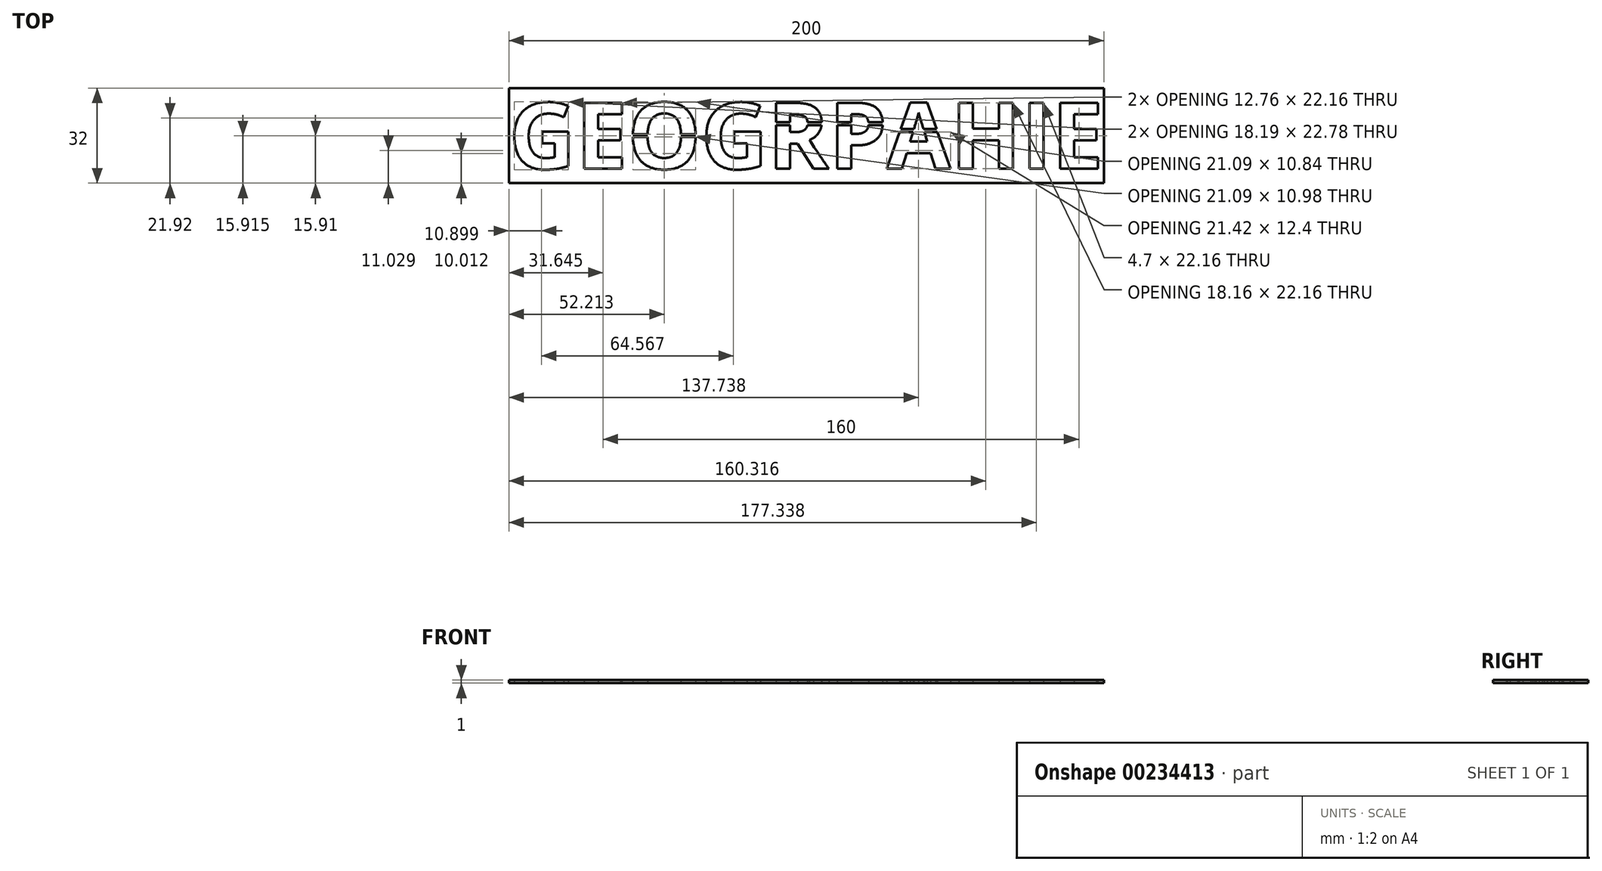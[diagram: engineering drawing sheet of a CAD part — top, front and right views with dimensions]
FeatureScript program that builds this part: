
annotation { "Feature Type Name" : "Feature", "Feature Type Description" : "" }
export const myFeature = defineFeature(function(context is Context, id is Id, definition is map)
    precondition{}
    {
        {
            var Q0;
            Q0=qCreatedBy(makeId("Top.planeOp"),FACE);
            var sketch = newSketch(context, id + "F0", { "sketchPlane" : qUnion([Q0])});
            skLineSegment(sketch, "E0.bottom", {"start": v(0, 0) * mm, "end": v(200, 0) * mm});
            skLineSegment(sketch, "E0.top", {"start": v(0, 32) * mm, "end": v(200, 32) * mm});
            skLineSegment(sketch, "E0.left", {"start": v(0, 0) * mm, "end": v(0, 32) * mm});
            skLineSegment(sketch, "E0.right", {"start": v(200, 0) * mm, "end": v(200, 32) * mm});
            skText(sketch, "E1", { "text": "GEOGRPAHIE", "fontName": "OpenSans-Bold.ttf"});
            skPoint(sketch, "E2", {"position": v(0, 16) * mm});
            skPoint(sketch, "E3", {"position": v(22.5, 32) * mm});
            skPoint(sketch, "E4", {"position": v(40, 32) * mm});
            skPoint(sketch, "E5", {"position": v(64.5, 32) * mm});
            skPoint(sketch, "E6", {"position": v(87, 32) * mm});
            skPoint(sketch, "E7", {"position": v(108.5, 32) * mm});
            skPoint(sketch, "E8", {"position": v(126.5, 32) * mm});
            skPoint(sketch, "E9", {"position": v(150, 32) * mm});
            skPoint(sketch, "E10", {"position": v(172, 32) * mm});
            skPoint(sketch, "E11", {"position": v(182.5, 32) * mm});
            skLineSegment(sketch, "E12", {"start": v(22.5, 32) * mm, "end": v(22.5, 0) * mm, "construction": true});
            skLineSegment(sketch, "E13", {"start": v(40, 32) * mm, "end": v(40, 0) * mm, "construction": true});
            skLineSegment(sketch, "E14", {"start": v(64.5, 32) * mm, "end": v(64.5, 0) * mm, "construction": true});
            skPoint(sketch, "E15", {"position": v(22.5, 16) * mm});
            skPoint(sketch, "E16", {"position": v(40, 16) * mm});
            skPoint(sketch, "E17", {"position": v(64.5, 16) * mm});
            skLineSegment(sketch, "E18", {"start": v(40, 16.5) * mm, "end": v(64.5, 16.5) * mm});
            skLineSegment(sketch, "E19", {"start": v(40, 16) * mm, "end": v(64.5, 16) * mm, "construction": true});
            skLineSegment(sketch, "E20.MirrorCS", {"start": v(40, 15.5) * mm, "end": v(64.5, 15.5) * mm});
            skLineSegment(sketch, "E21", {"start": v(87, 32) * mm, "end": v(87, 0) * mm, "construction": true});
            skLineSegment(sketch, "E22", {"start": v(108.5, 32) * mm, "end": v(108.5, 0) * mm, "construction": true});
            skLineSegment(sketch, "E23", {"start": v(126.5, 32) * mm, "end": v(126.5, 0) * mm, "construction": true});
            skLineSegment(sketch, "E24", {"start": v(150, 32) * mm, "end": v(150, 0) * mm, "construction": true});
            skLineSegment(sketch, "E25", {"start": v(172, 32) * mm, "end": v(172, 0) * mm, "construction": true});
            skLineSegment(sketch, "E26", {"start": v(182.5, 32) * mm, "end": v(182.5, 0) * mm, "construction": true});
            skLineSegment(sketch, "E27", {"start": v(87, 20.55) * mm, "end": v(108.5, 20.55) * mm});
            skLineSegment(sketch, "E28", {"start": v(87, 20.05) * mm, "end": v(108.5, 20.05) * mm, "construction": true});
            skLineSegment(sketch, "E29.MirrorCS", {"start": v(87, 19.55) * mm, "end": v(108.5, 19.55) * mm});
            skLineSegment(sketch, "E30", {"start": v(108.5, 19.97) * mm, "end": v(126.5, 19.97) * mm, "construction": true});
            skLineSegment(sketch, "E31", {"start": v(108.5, 20.47) * mm, "end": v(126.5, 20.47) * mm});
            skLineSegment(sketch, "E32.MirrorCS", {"start": v(108.5, 19.47) * mm, "end": v(126.5, 19.47) * mm});
            skLineSegment(sketch, "E33", {"start": v(126.5, 17.73) * mm, "end": v(150, 17.73) * mm, "construction": true});
            skLineSegment(sketch, "E34", {"start": v(126.5, 18.23) * mm, "end": v(150, 18.23) * mm});
            skLineSegment(sketch, "E35.MirrorCS", {"start": v(126.5, 17.23) * mm, "end": v(150, 17.23) * mm});
            const initialGuessF0  = {"E1": [0, 0.00483, 1, 0, 0.02235]};
            skSetInitialGuess(sketch, initialGuessF0);
            skSolve(sketch);
        }
        {
            var Q0;
            Q0 = qSketchRegion(id + "F0", true);
            var Q1;
            {var subQ8=sQuery(id+"F0.wireOp",EDGE,"E1.sketch_text.stroke-45");Q1=makeQuery(id+"F0.imprint","IMPRINT",FACE,{"disambiguationData":[TD([[makeQuery(id+"F0.imprint","IMPRINT",EDGE,{"derivedFrom":subQ8}),1.0]])]});}
            var Q2;
            {var subQ1=sQuery(id+"F0.wireOp",EDGE,"E1.sketch_text.stroke-67");Q2=makeQuery(id+"F0.imprint","IMPRINT",FACE,{"disambiguationData":[TD([[makeQuery(id+"F0.imprint","IMPRINT",EDGE,{"derivedFrom":subQ1}),1.0]])]});}
            var Q3;
            {var subQ1=sQuery(id+"F0.wireOp",EDGE,"E1.sketch_text.stroke-64");Q3=makeQuery(id+"F0.imprint","IMPRINT",FACE,{"disambiguationData":[TD([[makeQuery(id+"F0.imprint","IMPRINT",EDGE,{"derivedFrom":subQ1}),1.0]])]});}
            var Q4;
            Q4=makeQuery(id+"F0.imprint","IMPRINT",FACE,{"disambiguationData":[TD([[makeQuery(id+"F0.imprint","IMPRINT",EDGE,{"derivedFrom":sQuery(id+"F0.wireOp",EDGE,"E1.sketch_text.stroke-83")}),1.0]])]});
            var Q5;
            Q5=makeQuery(id+"F0.imprint","IMPRINT",FACE,{"disambiguationData":[TD([[makeQuery(id+"F0.imprint","IMPRINT",EDGE,{"derivedFrom":sQuery(id+"F0.wireOp",EDGE,"E1.sketch_text.stroke-107")}),1.0]])]});
            var Q6;
            {var subQ0=sQuery(id+"F0.wireOp",EDGE,"E1.sketch_text.stroke-38");var subQ1=sQuery(id+"F0.wireOp",EDGE,"E1.sketch_text.stroke-31");var subQ2=makeQuery(id+"F0.imprint","INTERSECT",VERTEX,{"derivedFrom":[subQ1,subQ0]});Q6=makeQuery(id+"F0.imprint","IMPRINT",FACE,{"disambiguationData":[TD([[makeQuery(id+"F0.imprint","IMPRINT",EDGE,{"disambiguationData":[TD([[subQ2,-1.0]])],"derivedFrom":subQ1}),1.0]])]});}
            var Q7;
            {var subQ0=sQuery(id+"F0.wireOp",EDGE,"E1.sketch_text.stroke-59");Q7=makeQuery(id+"F0.imprint","IMPRINT",FACE,{"disambiguationData":[TD([[makeQuery(id+"F0.imprint","IMPRINT",EDGE,{"derivedFrom":subQ0}),1.0]])]});}
            var Q8;
            {var subQ9=sQuery(id+"F0.wireOp",EDGE,"E1.sketch_text.stroke-27");Q8=makeQuery(id+"F0.imprint","IMPRINT",FACE,{"disambiguationData":[TD([[makeQuery(id+"F0.imprint","IMPRINT",EDGE,{"derivedFrom":subQ9}),1.0]])]});}
            var Q9;
            {var subQ11=sQuery(id+"F0.wireOp",EDGE,"E1.sketch_text.stroke-0");Q9=makeQuery(id+"F0.imprint","IMPRINT",FACE,{"disambiguationData":[TD([[makeQuery(id+"F0.imprint","IMPRINT",EDGE,{"derivedFrom":subQ11}),1.0]])]});}
            var Q10;
            {var subQ5=sQuery(id+"F0.wireOp",EDGE,"E1.sketch_text.stroke-14");Q10=makeQuery(id+"F0.imprint","IMPRINT",FACE,{"disambiguationData":[TD([[makeQuery(id+"F0.imprint","IMPRINT",EDGE,{"derivedFrom":subQ5}),1.0]])]});}
            var Q11;
            {var subQ0=sQuery(id+"F0.wireOp",EDGE,"E1.sketch_text.stroke-44");var subQ1=sQuery(id+"F0.wireOp",EDGE,"E1.sketch_text.stroke-39");var subQ2=makeQuery(id+"F0.imprint","INTERSECT",VERTEX,{"derivedFrom":[subQ1,subQ0]});Q11=makeQuery(id+"F0.imprint","IMPRINT",FACE,{"disambiguationData":[TD([[makeQuery(id+"F0.imprint","IMPRINT",EDGE,{"disambiguationData":[TD([[subQ2,-1.0]])],"derivedFrom":subQ1}),1.0]])]});}
            var Q12;
            {var subQ0=sQuery(id+"F0.wireOp",EDGE,"E1.sketch_text.stroke-43");Q12=makeQuery(id+"F0.imprint","IMPRINT",FACE,{"disambiguationData":[TD([[makeQuery(id+"F0.imprint","IMPRINT",EDGE,{"derivedFrom":subQ0}),1.0]])]});}
            var Q13;
            {var subQ0=sQuery(id+"F0.wireOp",EDGE,"E1.sketch_text.stroke-40");Q13=makeQuery(id+"F0.imprint","IMPRINT",FACE,{"disambiguationData":[TD([[makeQuery(id+"F0.imprint","IMPRINT",EDGE,{"derivedFrom":subQ0}),1.0]])]});}
            var Q14;
            {var subQ1=sQuery(id+"F0.wireOp",EDGE,"E1.sketch_text.stroke-12");var subQ5=sQuery(id+"F0.wireOp",EDGE,"E1.sketch_text.stroke-13");var subQ6=makeQuery(id+"F0.imprint","INTERSECT",VERTEX,{"derivedFrom":[subQ1,subQ5]});Q14=makeQuery(id+"F0.imprint","IMPRINT",FACE,{"disambiguationData":[TD([[makeQuery(id+"F0.imprint","IMPRINT",EDGE,{"disambiguationData":[TD([[subQ6,1.0]])],"derivedFrom":subQ1}),1.0]])]});}
            var Q15;
            {var subQ0=sQuery(id+"F0.wireOp",EDGE,"Y53SOWeo-wKMP-z9sr-oB1W-zrnG9GxjqqMA");var subQ1=sQuery(id+"F0.wireOp",EDGE,"E1.sketch_text.stroke-1");var subQ2=makeQuery(id+"F0.imprint","INTERSECT",VERTEX,{"derivedFrom":[subQ1,subQ0]});Q15=makeQuery(id+"F0.imprint","IMPRINT",FACE,{"disambiguationData":[TD([[makeQuery(id+"F0.imprint","IMPRINT",EDGE,{"disambiguationData":[TD([[subQ2,-1.0]])],"derivedFrom":subQ1}),1.0]])]});}
            var Q16;
            {var subQ3=sQuery(id+"F0.wireOp",EDGE,"Y53SOWeo-wKMP-z9sr-oB1W-zrnG9GxjqqMA");var subQ6=sQuery(id+"F0.wireOp",EDGE,"E1.sketch_text.stroke-26");var subQ9=makeQuery(id+"F0.imprint","INTERSECT",VERTEX,{"derivedFrom":[subQ6,subQ3]});Q16=makeQuery(id+"F0.imprint","IMPRINT",FACE,{"disambiguationData":[TD([[makeQuery(id+"F0.imprint","IMPRINT",EDGE,{"disambiguationData":[TD([[subQ9,-1.0]])],"derivedFrom":subQ6}),1.0]])]});}
            var Q17;
            {var subQ1=sQuery(id+"F0.wireOp",EDGE,"E1.sketch_text.stroke-57");var subQ7=sQuery(id+"F0.wireOp",EDGE,"E1.sketch_text.stroke-58");var subQ8=makeQuery(id+"F0.imprint","INTERSECT",VERTEX,{"derivedFrom":[subQ1,subQ7]});Q17=makeQuery(id+"F0.imprint","IMPRINT",FACE,{"disambiguationData":[TD([[makeQuery(id+"F0.imprint","IMPRINT",EDGE,{"disambiguationData":[TD([[subQ8,1.0]])],"derivedFrom":subQ1}),1.0]])]});}
            var Q18;
            {var subQ0=sQuery(id+"F0.wireOp",EDGE,"Y53SOWeo-wKMP-z9sr-oB1W-zrnG9GxjqqMA");var subQ1=sQuery(id+"F0.wireOp",EDGE,"E1.sketch_text.stroke-46");var subQ2=makeQuery(id+"F0.imprint","INTERSECT",VERTEX,{"derivedFrom":[subQ1,subQ0]});Q18=makeQuery(id+"F0.imprint","IMPRINT",FACE,{"disambiguationData":[TD([[makeQuery(id+"F0.imprint","IMPRINT",EDGE,{"disambiguationData":[TD([[subQ2,-1.0]])],"derivedFrom":subQ1}),1.0]])]});}
            var Q19;
            {var subQ0=sQuery(id+"F0.wireOp",EDGE,"E1.sketch_text.stroke-38");var subQ1=sQuery(id+"F0.wireOp",EDGE,"E1.sketch_text.stroke-31");var subQ2=makeQuery(id+"F0.imprint","INTERSECT",VERTEX,{"derivedFrom":[subQ1,subQ0]});Q19=makeQuery(id+"F0.imprint","IMPRINT",FACE,{"disambiguationData":[TD([[makeQuery(id+"F0.imprint","IMPRINT",EDGE,{"disambiguationData":[TD([[subQ2,-1.0]])],"derivedFrom":subQ1}),-1.0]])]});}
            var Q20;
            {var subQ5=sQuery(id+"F0.wireOp",EDGE,"E1.sketch_text.stroke-35");var subQ6=sQuery(id+"F0.wireOp",EDGE,"E1.sketch_text.stroke-34");var subQ7=makeQuery(id+"F0.imprint","INTERSECT",VERTEX,{"derivedFrom":[subQ6,subQ5]});Q20=makeQuery(id+"F0.imprint","IMPRINT",FACE,{"disambiguationData":[TD([[makeQuery(id+"F0.imprint","IMPRINT",EDGE,{"disambiguationData":[TD([[subQ7,1.0]])],"derivedFrom":subQ6}),-1.0]])]});}
            var Q21;
            {var subQ0=sQuery(id+"F0.wireOp",EDGE,"E27");var subQ1=sQuery(id+"F0.wireOp",EDGE,"E1.sketch_text.stroke-70");var subQ2=makeQuery(id+"F0.imprint","INTERSECT",VERTEX,{"derivedFrom":[subQ1,subQ0]});Q21=makeQuery(id+"F0.imprint","IMPRINT",FACE,{"disambiguationData":[TD([[makeQuery(id+"F0.imprint","IMPRINT",EDGE,{"disambiguationData":[TD([[subQ2,-1.0]])],"derivedFrom":subQ1}),-1.0]])]});}
            var Q22;
            {var subQ3=sQuery(id+"F0.wireOp",EDGE,"E1.sketch_text.stroke-67");var subQ7=sQuery(id+"F0.wireOp",EDGE,"E1.sketch_text.stroke-66");var subQ8=makeQuery(id+"F0.imprint","INTERSECT",VERTEX,{"derivedFrom":[subQ7,subQ3]});Q22=makeQuery(id+"F0.imprint","IMPRINT",FACE,{"disambiguationData":[TD([[makeQuery(id+"F0.imprint","IMPRINT",EDGE,{"disambiguationData":[TD([[subQ8,1.0]])],"derivedFrom":subQ7}),-1.0]])]});}
            var Q23;
            {var subQ1=sQuery(id+"F0.wireOp",EDGE,"E1.sketch_text.stroke-86");var subQ7=sQuery(id+"F0.wireOp",EDGE,"E1.sketch_text.stroke-85");var subQ8=makeQuery(id+"F0.imprint","INTERSECT",VERTEX,{"derivedFrom":[subQ7,subQ1]});Q23=makeQuery(id+"F0.imprint","IMPRINT",FACE,{"disambiguationData":[TD([[makeQuery(id+"F0.imprint","IMPRINT",EDGE,{"disambiguationData":[TD([[subQ8,1.0]])],"derivedFrom":subQ7}),1.0]])]});}
            var Q24;
            {var subQ6=sQuery(id+"F0.wireOp",EDGE,"E1.sketch_text.stroke-87");Q24=makeQuery(id+"F0.imprint","IMPRINT",FACE,{"disambiguationData":[TD([[makeQuery(id+"F0.imprint","IMPRINT",EDGE,{"derivedFrom":subQ6}),1.0]])]});}
            var Q25;
            {var subQ0=sQuery(id+"F0.wireOp",EDGE,"E31");var subQ1=sQuery(id+"F0.wireOp",EDGE,"E1.sketch_text.stroke-89");var subQ2=makeQuery(id+"F0.imprint","INTERSECT",VERTEX,{"derivedFrom":[subQ1,subQ0]});Q25=makeQuery(id+"F0.imprint","IMPRINT",FACE,{"disambiguationData":[TD([[makeQuery(id+"F0.imprint","IMPRINT",EDGE,{"disambiguationData":[TD([[subQ2,-1.0]])],"derivedFrom":subQ1}),-1.0]])]});}
            var Q26;
            {var subQ5=sQuery(id+"F0.wireOp",EDGE,"E1.sketch_text.stroke-86");var subQ6=sQuery(id+"F0.wireOp",EDGE,"E1.sketch_text.stroke-85");var subQ7=makeQuery(id+"F0.imprint","INTERSECT",VERTEX,{"derivedFrom":[subQ6,subQ5]});Q26=makeQuery(id+"F0.imprint","IMPRINT",FACE,{"disambiguationData":[TD([[makeQuery(id+"F0.imprint","IMPRINT",EDGE,{"disambiguationData":[TD([[subQ7,1.0]])],"derivedFrom":subQ6}),-1.0]])]});}
            var Q27;
            {var subQ0=sQuery(id+"F0.wireOp",EDGE,"E35.MirrorCS");var subQ1=sQuery(id+"F0.wireOp",EDGE,"E1.sketch_text.stroke-103");var subQ2=makeQuery(id+"F0.imprint","INTERSECT",VERTEX,{"derivedFrom":[subQ1,subQ0]});Q27=makeQuery(id+"F0.imprint","IMPRINT",FACE,{"disambiguationData":[TD([[makeQuery(id+"F0.imprint","IMPRINT",EDGE,{"disambiguationData":[TD([[subQ2,-1.0]])],"derivedFrom":subQ1}),-1.0]])]});}
            var Q28;
            {var subQ0=sQuery(id+"F0.wireOp",EDGE,"E34");var subQ1=sQuery(id+"F0.wireOp",EDGE,"E1.sketch_text.stroke-105");var subQ2=makeQuery(id+"F0.imprint","INTERSECT",VERTEX,{"derivedFrom":[subQ1,subQ0]});Q28=makeQuery(id+"F0.imprint","IMPRINT",FACE,{"disambiguationData":[TD([[makeQuery(id+"F0.imprint","IMPRINT",EDGE,{"disambiguationData":[TD([[subQ2,-1.0]])],"derivedFrom":subQ1}),-1.0]])]});}
            extrude(context, id + "F1", {"entities" : qUnion([Q0, Q1, Q2, Q3, Q4, Q5, Q6, Q7, Q8, Q9, Q10, Q11, Q12, Q13, Q14, Q15, Q16, Q17, Q18, Q19, Q20, Q21, Q22, Q23, Q24, Q25, Q26, Q27, Q28]), "depth" : 1 * mm});
        }
    });
